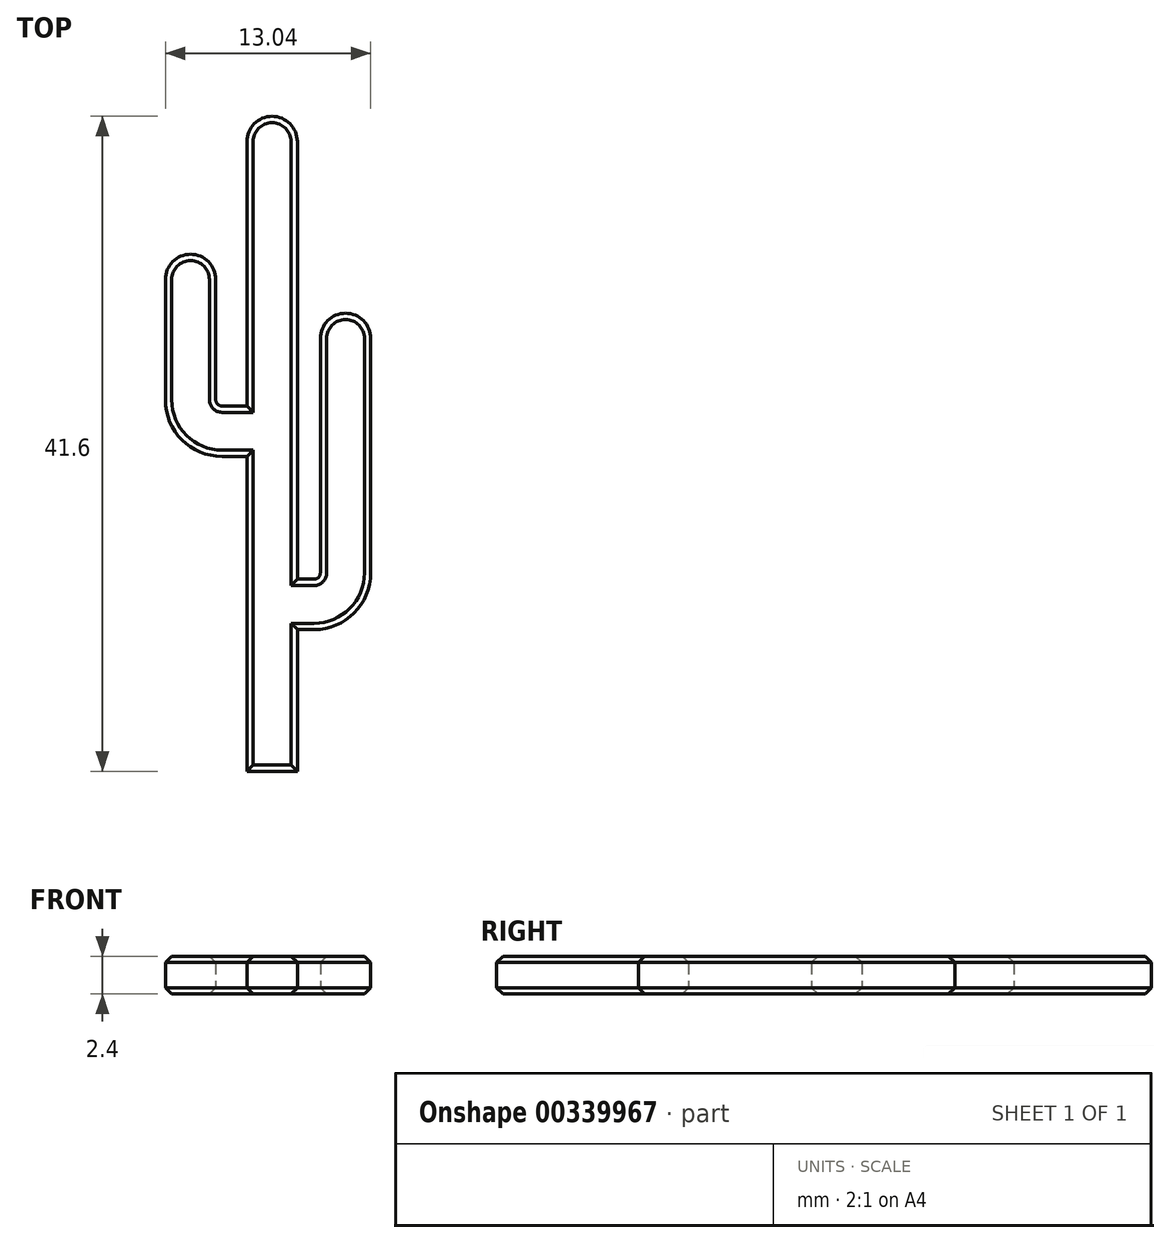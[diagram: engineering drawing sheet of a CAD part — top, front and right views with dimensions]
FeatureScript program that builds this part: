
annotation { "Feature Type Name" : "Feature", "Feature Type Description" : "" }
export const myFeature = defineFeature(function(context is Context, id is Id, definition is map)
    precondition{}
    {
        {
            var Q0;
            Q0=qCreatedBy(makeId("Top.planeOp"),FACE);
            var sketch = newSketch(context, id + "F0", { "sketchPlane" : qUnion([Q0])});
            skCircle(sketch, "E0", {"center": v(0, 0) * mm, "radius": 1.6 * mm});
            skLineSegment(sketch, "E1.bottom", {"start": v(-1.6, 0) * mm, "end": v(1.6, 0) * mm});
            skLineSegment(sketch, "E1.top", {"start": v(-1.6, -40) * mm, "end": v(1.6, -40) * mm});
            skLineSegment(sketch, "E1.left", {"start": v(-1.6, 0) * mm, "end": v(-1.6, -40) * mm});
            skLineSegment(sketch, "E1.right", {"start": v(1.6, 0) * mm, "end": v(1.6, -40) * mm});
            skLineSegment(sketch, "E2.bottom", {"start": v(1.6, -27.8) * mm, "end": v(3.06, -27.8) * mm});
            skLineSegment(sketch, "E2.top", {"start": v(1.6, -31) * mm, "end": v(3.06, -31) * mm});
            skLineSegment(sketch, "E2.left", {"start": v(1.6, -27.8) * mm, "end": v(1.6, -31) * mm});
            skLineSegment(sketch, "E2.right", {"start": v(3.06, -27.8) * mm, "end": v(3.06, -31) * mm});
            skLineSegment(sketch, "E3.bottom", {"start": v(3.06, -31) * mm, "end": v(6.26, -31) * mm});
            skLineSegment(sketch, "E3.top", {"start": v(3.06, -12.5) * mm, "end": v(6.26, -12.5) * mm});
            skLineSegment(sketch, "E3.left", {"start": v(3.06, -31) * mm, "end": v(3.06, -12.5) * mm});
            skLineSegment(sketch, "E3.right", {"start": v(6.26, -31) * mm, "end": v(6.26, -12.5) * mm});
            skCircle(sketch, "E4", {"center": v(4.66, -12.5) * mm, "radius": 1.6 * mm});
            skLineSegment(sketch, "E5.bottom", {"start": v(-1.6, -20) * mm, "end": v(-3.58, -20) * mm});
            skLineSegment(sketch, "E5.top", {"start": v(-1.6, -16.8) * mm, "end": v(-3.58, -16.8) * mm});
            skLineSegment(sketch, "E5.left", {"start": v(-1.6, -20) * mm, "end": v(-1.6, -16.8) * mm});
            skLineSegment(sketch, "E5.right", {"start": v(-3.58, -20) * mm, "end": v(-3.58, -16.8) * mm});
            skLineSegment(sketch, "E6.bottom", {"start": v(-3.58, -20) * mm, "end": v(-6.78, -20) * mm});
            skLineSegment(sketch, "E6.top", {"start": v(-3.58, -8.76) * mm, "end": v(-6.78, -8.76) * mm});
            skLineSegment(sketch, "E6.left", {"start": v(-3.58, -20) * mm, "end": v(-3.58, -8.76) * mm});
            skLineSegment(sketch, "E6.right", {"start": v(-6.78, -20) * mm, "end": v(-6.78, -8.76) * mm});
            skCircle(sketch, "E7", {"center": v(-5.18, -8.76) * mm, "radius": 1.6 * mm});
            skSolve(sketch);
        }
        {
            var Q0;
            Q0=qSketchRegion(id+"F0",true);
            extrude(context, id + "F1", {"entities" : qUnion([Q0]), "depth" : 2.4 * mm, "offsetDistance" : 25 * mm});
        }
        {
            var Q0;
            Q0=makeQuery(id+"F1.opExtrude","SWEPT_EDGE",EDGE,{"disambiguationData":[OSD([sQuery(id+"F0.wireOp",EDGE,"E6.bottom"),sQuery(id+"F0.wireOp",EDGE,"E6.right")])]});
            var Q1;
            Q1=makeQuery(id+"F1.opExtrude","SWEPT_EDGE",EDGE,{"disambiguationData":[OSD([sQuery(id+"F0.wireOp",EDGE,"E3.bottom"),sQuery(id+"F0.wireOp",EDGE,"E3.right")])]});
            fillet(context, id + "F2", {"entities" : qUnion([Q0, Q1]), "radius" : 3.6 * mm, "tangentPropagation" : true, "allowEdgeOverflow" : false});
        }
        {
            var Q0;
            Q0=makeQuery(id+"F1.opExtrude","SWEPT_EDGE",EDGE,{"disambiguationData":[OSD([sQuery(id+"F0.wireOp",EDGE,"E5.top"),sQuery(id+"F0.wireOp",EDGE,"E6.left")])]});
            var Q1;
            Q1=makeQuery(id+"F1.opExtrude","SWEPT_EDGE",EDGE,{"disambiguationData":[OSD([sQuery(id+"F0.wireOp",EDGE,"E2.bottom"),sQuery(id+"F0.wireOp",EDGE,"E3.left")])]});
            fillet(context, id + "F3", {"entities" : qUnion([Q0, Q1]), "radius" : 0.4 * mm, "tangentPropagation" : true, "allowEdgeOverflow" : false});
        }
        {
            var Q0;
            Q0=makeQuery(id+"F1.opExtrude","CAP_FACE",FACE,{"disambiguationData":[OSD([sQuery(id+"F0.wireOp",EDGE,"E0"),sQuery(id+"F0.wireOp",EDGE,"E1.top"),sQuery(id+"F0.wireOp",EDGE,"E1.left"),sQuery(id+"F0.wireOp",EDGE,"E1.right"),sQuery(id+"F0.wireOp",EDGE,"E2.bottom"),sQuery(id+"F0.wireOp",EDGE,"E2.top"),sQuery(id+"F0.wireOp",EDGE,"E3.bottom"),sQuery(id+"F0.wireOp",EDGE,"E3.left"),sQuery(id+"F0.wireOp",EDGE,"E3.right"),sQuery(id+"F0.wireOp",EDGE,"E4"),sQuery(id+"F0.wireOp",EDGE,"E5.bottom"),sQuery(id+"F0.wireOp",EDGE,"E5.top"),sQuery(id+"F0.wireOp",EDGE,"E6.bottom"),sQuery(id+"F0.wireOp",EDGE,"E6.left"),sQuery(id+"F0.wireOp",EDGE,"E6.right"),sQuery(id+"F0.wireOp",EDGE,"E7")])],"isStart":false});
            var Q1;
            Q1=makeQuery(id+"F1.opExtrude","CAP_FACE",FACE,{"disambiguationData":[OSD([sQuery(id+"F0.wireOp",EDGE,"E0"),sQuery(id+"F0.wireOp",EDGE,"E1.top"),sQuery(id+"F0.wireOp",EDGE,"E1.left"),sQuery(id+"F0.wireOp",EDGE,"E1.right"),sQuery(id+"F0.wireOp",EDGE,"E2.bottom"),sQuery(id+"F0.wireOp",EDGE,"E2.top"),sQuery(id+"F0.wireOp",EDGE,"E3.bottom"),sQuery(id+"F0.wireOp",EDGE,"E3.left"),sQuery(id+"F0.wireOp",EDGE,"E3.right"),sQuery(id+"F0.wireOp",EDGE,"E4"),sQuery(id+"F0.wireOp",EDGE,"E5.bottom"),sQuery(id+"F0.wireOp",EDGE,"E5.top"),sQuery(id+"F0.wireOp",EDGE,"E6.bottom"),sQuery(id+"F0.wireOp",EDGE,"E6.left"),sQuery(id+"F0.wireOp",EDGE,"E6.right"),sQuery(id+"F0.wireOp",EDGE,"E7")])],"isStart":true});
            chamfer(context, id + "F4", {"entities" : qUnion([Q0, Q1]), "width" : 0.4 * mm, "tangentPropagation" : true});
        }
    });
